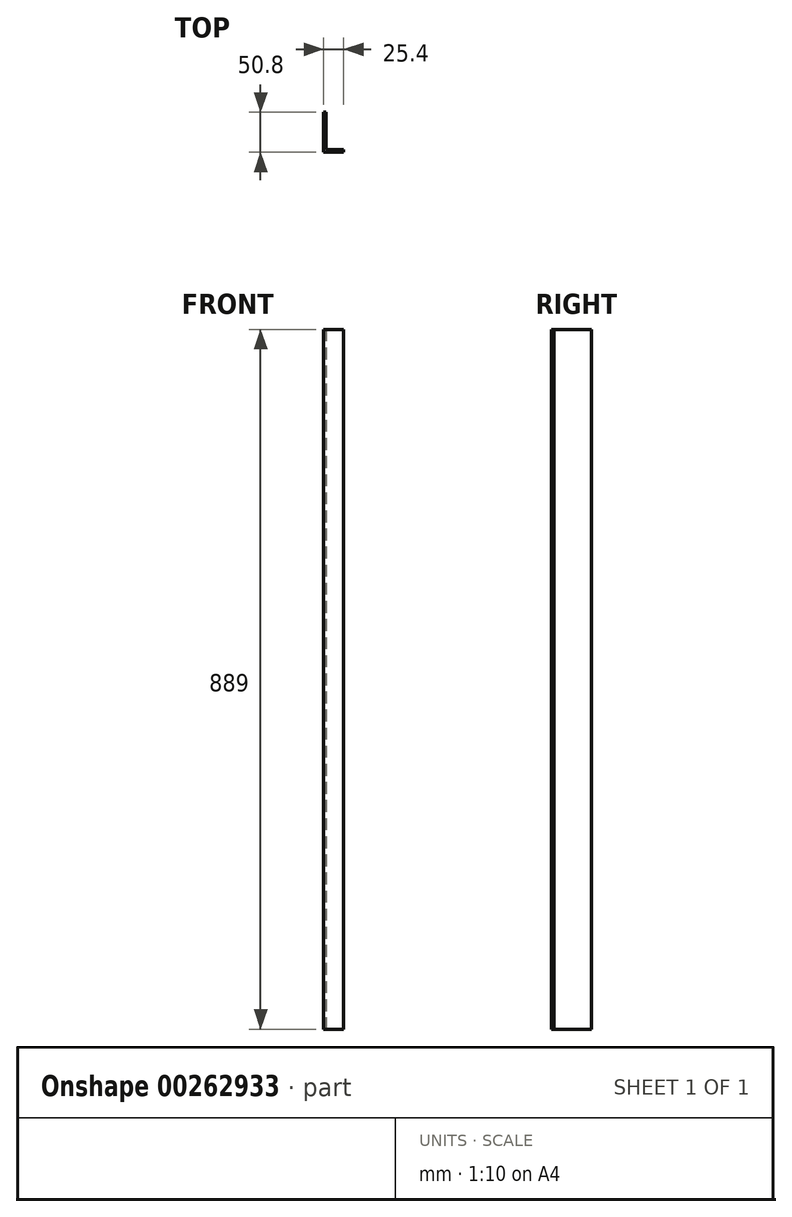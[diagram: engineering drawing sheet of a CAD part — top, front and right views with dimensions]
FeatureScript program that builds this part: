
annotation { "Feature Type Name" : "Feature", "Feature Type Description" : "" }
export const myFeature = defineFeature(function(context is Context, id is Id, definition is map)
    precondition{}
    {
        {
            var Q0;
            Q0=qCreatedBy(makeId("Top.planeOp"),FACE);
            var sketch = newSketch(context, id + "F0", { "sketchPlane" : qUnion([Q0])});
            skLineSegment(sketch, "E0", {"start": v(0, 50.8) * mm, "end": v(0, 0) * mm});
            skLineSegment(sketch, "E1", {"start": v(0, 0) * mm, "end": v(25.4, 0) * mm});
            skLineSegment(sketch, "E2", {"start": v(25.4, 0) * mm, "end": v(25.4, 3.18) * mm});
            skLineSegment(sketch, "E3", {"start": v(25.4, 3.18) * mm, "end": v(3.18, 3.17) * mm});
            skLineSegment(sketch, "E4", {"start": v(3.17, 3.18) * mm, "end": v(3.17, 50.8) * mm});
            skLineSegment(sketch, "E5", {"start": v(3.17, 50.8) * mm, "end": v(0, 50.8) * mm});
            skSolve(sketch);
        }
        {
            var Q0;
            Q0 = qSketchRegion(id + "F0", true);
            extrude(context, id + "F1", {"entities" : qUnion([Q0]), "depth" : 889 * mm});
        }
    });
